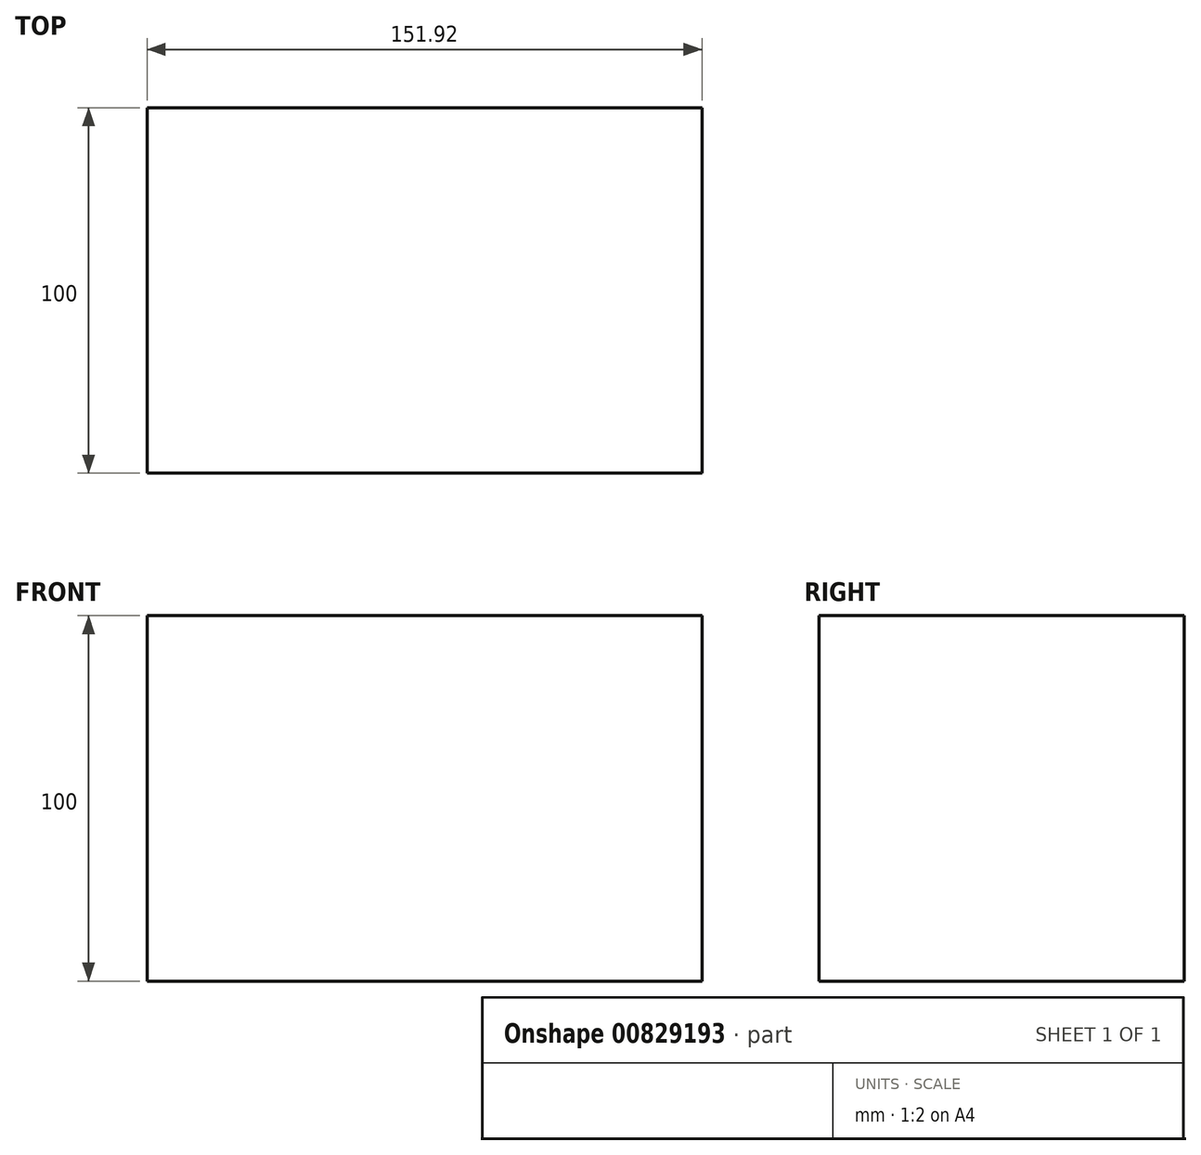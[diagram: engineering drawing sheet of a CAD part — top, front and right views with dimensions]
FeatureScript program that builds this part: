
annotation { "Feature Type Name" : "Feature", "Feature Type Description" : "" }
export const myFeature = defineFeature(function(context is Context, id is Id, definition is map)
    precondition{}
    {
        {
            var Q0;
            Q0=qCreatedBy(makeId("Top.planeOp"),FACE);
            var sketch = newSketch(context, id + "F0", { "sketchPlane" : qUnion([Q0])});
            skLineSegment(sketch, "E0.bottom", {"start": v(-75.23, 75.03) * mm, "end": v(75.23, 75.03) * mm});
            skLineSegment(sketch, "E0.top", {"start": v(-75.23, -75.03) * mm, "end": v(75.23, -75.03) * mm});
            skLineSegment(sketch, "E0.left", {"start": v(-75.23, 75.03) * mm, "end": v(-75.23, -75.03) * mm});
            skLineSegment(sketch, "E0.right", {"start": v(75.23, 75.03) * mm, "end": v(75.23, -75.03) * mm});
            skPoint(sketch, "E0.middle", {"position": v(0, 0) * mm});
            skSolve(sketch);
        }
        {
            var Q0;
            Q0=makeQuery(id+"F0.imprint","IMPRINT",FACE,{"disambiguationData":[TD([[makeQuery(id+"F0.imprint","IMPRINT",EDGE,{"derivedFrom":sQuery(id+"F0.wireOp",EDGE,"E0.bottom")}),-1.0]])]});
            var sketch = newSketch(context, id + "F1", { "sketchPlane" : qUnion([Q0])});
            skLineSegment(sketch, "E1.bottom", {"start": v(-75.96, 50) * mm, "end": v(75.96, 50) * mm});
            skLineSegment(sketch, "E1.top", {"start": v(-75.96, -50) * mm, "end": v(75.96, -50) * mm});
            skLineSegment(sketch, "E1.left", {"start": v(-75.96, 50) * mm, "end": v(-75.96, -50) * mm});
            skLineSegment(sketch, "E1.right", {"start": v(75.96, 50) * mm, "end": v(75.96, -50) * mm});
            skPoint(sketch, "E1.middle", {"position": v(0, 0) * mm});
            skSolve(sketch);
        }
        {
            var Q0;
            Q0 = qSketchRegion(id + "F1", true);
            extrude(context, id + "F2", {"entities" : qUnion([Q0]), "depth" : 100 * mm, "offsetDistance" : 25 * mm});
        }
    });
